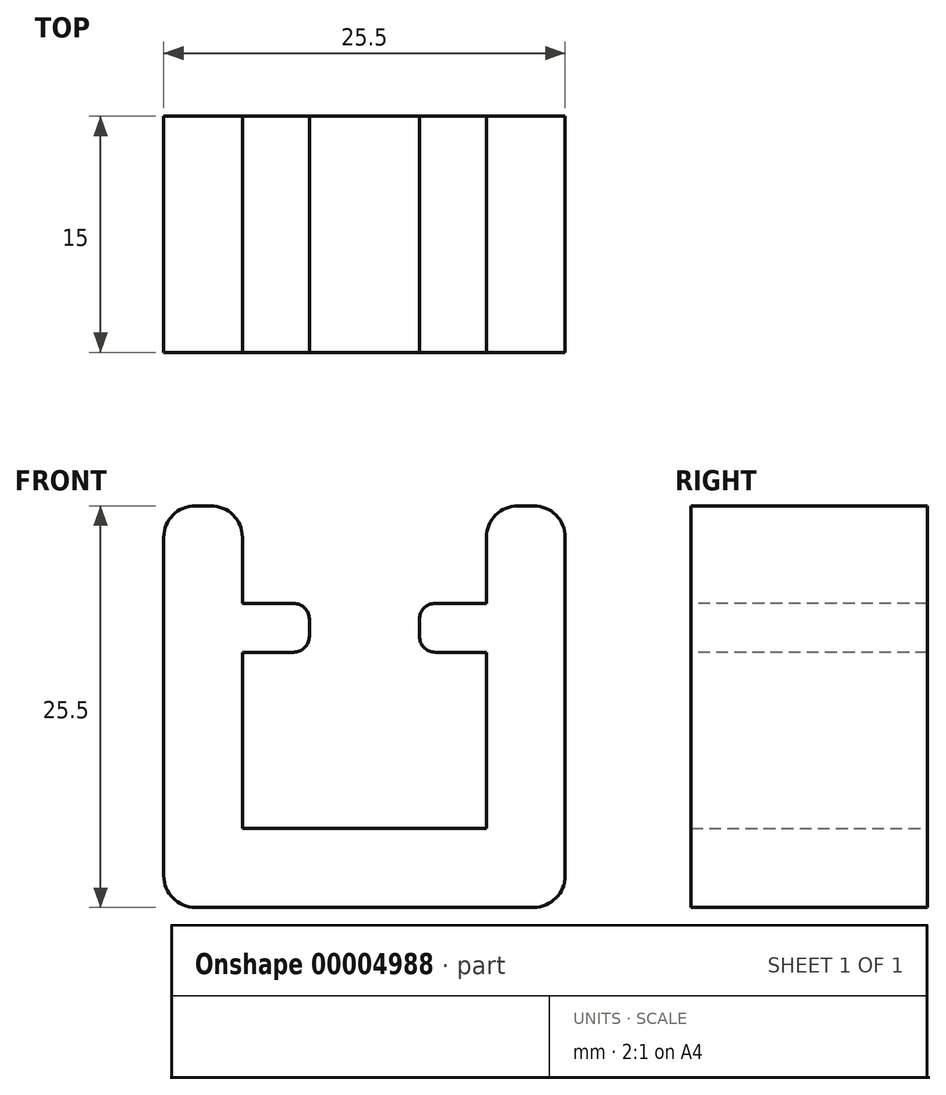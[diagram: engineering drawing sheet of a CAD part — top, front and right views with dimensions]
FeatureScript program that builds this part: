
annotation { "Feature Type Name" : "Feature", "Feature Type Description" : "" }
export const myFeature = defineFeature(function(context is Context, id is Id, definition is map)
    precondition{}
    {
        {
            var Q0;
            Q0=qCreatedBy(makeId("Front.planeOp"),FACE);
            var sketch = newSketch(context, id + "F0", { "sketchPlane" : qUnion([Q0])});
            skLineSegment(sketch, "E0", {"start": v(0, 0) * mm, "end": v(0, 15.32) * mm, "construction": true});
            skLineSegment(sketch, "E1.rect.bottom", {"start": v(7.75, 7.75) * mm, "end": v(-7.75, 7.75) * mm, "construction": true});
            skLineSegment(sketch, "E1.rect.top", {"start": v(7.75, -7.75) * mm, "end": v(-7.75, -7.75) * mm, "construction": true});
            skLineSegment(sketch, "E1.rect.left", {"start": v(7.75, 7.75) * mm, "end": v(7.75, -7.75) * mm});
            skLineSegment(sketch, "E1.rect.right", {"start": v(-7.75, 7.75) * mm, "end": v(-7.75, -7.75) * mm});
            skPoint(sketch, "E1.rect.middle", {"position": v(0, 0) * mm});
            skLineSegment(sketch, "E2", {"start": v(-7.75, 7.75) * mm, "end": v(-12.75, 7.75) * mm});
            skLineSegment(sketch, "E3", {"start": v(-12.75, 7.75) * mm, "end": v(-12.75, -17.75) * mm});
            skLineSegment(sketch, "E4", {"start": v(7.75, 7.75) * mm, "end": v(12.75, 7.75) * mm});
            skLineSegment(sketch, "E5", {"start": v(12.75, 7.75) * mm, "end": v(12.75, -17.75) * mm});
            skLineSegment(sketch, "E6", {"start": v(12.75, -17.75) * mm, "end": v(-12.75, -17.75) * mm});
            skLineSegment(sketch, "E7", {"start": v(-7.75, -7.75) * mm, "end": v(-7.75, -12.75) * mm});
            skLineSegment(sketch, "E8", {"start": v(-7.75, -12.75) * mm, "end": v(7.75, -12.75) * mm});
            skLineSegment(sketch, "E9", {"start": v(7.75, -12.75) * mm, "end": v(7.75, -7.75) * mm});
            skSolve(sketch);
        }
        {
            var Q0;
            Q0 = qSketchRegion(id + "F0", true);
            extrude(context, id + "F1", {"entities" : qUnion([Q0]), "depth" : 15 * mm});
        }
        {
            var Q0;
            Q0=makeQuery(id+"F1.opExtrude","CAP_FACE",FACE,{"disambiguationData":[OSD([sQuery(id+"F0.wireOp",EDGE,"E1.rect.left"),sQuery(id+"F0.wireOp",EDGE,"E1.rect.right"),sQuery(id+"F0.wireOp",EDGE,"E2"),sQuery(id+"F0.wireOp",EDGE,"E3"),sQuery(id+"F0.wireOp",EDGE,"E4"),sQuery(id+"F0.wireOp",EDGE,"E5"),sQuery(id+"F0.wireOp",EDGE,"E6"),sQuery(id+"F0.wireOp",EDGE,"E7"),sQuery(id+"F0.wireOp",EDGE,"E8"),sQuery(id+"F0.wireOp",EDGE,"E9")])],"isStart":false});
            var sketch = newSketch(context, id + "F2", { "sketchPlane" : qUnion([Q0])});
            skLineSegment(sketch, "E10", {"start": v(0, 0) * mm, "end": v(-7.75, 0) * mm, "construction": true});
            skLineSegment(sketch, "E11.bottom", {"start": v(-7.75, 1.55) * mm, "end": v(-3.5, 1.55) * mm});
            skLineSegment(sketch, "E11.top", {"start": v(-7.75, -1.55) * mm, "end": v(-3.5, -1.55) * mm});
            skLineSegment(sketch, "E11.left", {"start": v(-7.75, 1.55) * mm, "end": v(-7.75, -1.55) * mm});
            skLineSegment(sketch, "E11.right", {"start": v(-3.5, 1.55) * mm, "end": v(-3.5, -1.55) * mm});
            skPoint(sketch, "E12", {"position": v(-3.5, 0) * mm});
            skLineSegment(sketch, "E13", {"start": v(0, 0) * mm, "end": v(0, 15.8) * mm, "construction": true});
            skLineSegment(sketch, "E14.0.MirrorCS", {"start": v(7.75, -1.55) * mm, "end": v(3.5, -1.55) * mm});
            skLineSegment(sketch, "E14.1.MirrorCS", {"start": v(3.5, 1.55) * mm, "end": v(3.5, -1.55) * mm});
            skLineSegment(sketch, "E14.2.MirrorCS", {"start": v(7.75, 1.55) * mm, "end": v(7.75, -1.55) * mm});
            skLineSegment(sketch, "E14.3.MirrorCS", {"start": v(7.75, 1.55) * mm, "end": v(3.5, 1.55) * mm});
            skSolve(sketch);
        }
        {
            var Q0;
            Q0 = qSketchRegion(id + "F2", true);
            var Q1;
            Q1=makeQuery(id+"F1.opExtrude","CAP_FACE",FACE,{"disambiguationData":[OSD([sQuery(id+"F0.wireOp",EDGE,"E1.rect.left"),sQuery(id+"F0.wireOp",EDGE,"E1.rect.right"),sQuery(id+"F0.wireOp",EDGE,"E2"),sQuery(id+"F0.wireOp",EDGE,"E3"),sQuery(id+"F0.wireOp",EDGE,"E4"),sQuery(id+"F0.wireOp",EDGE,"E5"),sQuery(id+"F0.wireOp",EDGE,"E6"),sQuery(id+"F0.wireOp",EDGE,"E7"),sQuery(id+"F0.wireOp",EDGE,"E8"),sQuery(id+"F0.wireOp",EDGE,"E9")])],"isStart":true});
            extrude(context, id + "F3", {"entities" : qUnion([Q0]), "operationType" : NewBodyOperationType.ADD, "endBound" : BoundingType.UP_TO_SURFACE, "oppositeDirection" : true, "endBoundEntityFace" : qUnion([Q1]), "depth" : 25 * mm});
        }
        {
            var Q0;
            Q0=makeQuery(id+"F1.opExtrude","SWEPT_EDGE",EDGE,{"disambiguationData":[OSD([sQuery(id+"F0.wireOp",EDGE,"E3"),sQuery(id+"F0.wireOp",EDGE,"E6")])]});
            var Q1;
            Q1=makeQuery(id+"F1.opExtrude","SWEPT_EDGE",EDGE,{"disambiguationData":[OSD([sQuery(id+"F0.wireOp",EDGE,"E5"),sQuery(id+"F0.wireOp",EDGE,"E6")])]});
            var Q2;
            Q2=makeQuery(id+"F1.opExtrude","SWEPT_EDGE",EDGE,{"disambiguationData":[OSD([sQuery(id+"F0.wireOp",EDGE,"E4"),sQuery(id+"F0.wireOp",EDGE,"E5")])]});
            var Q3;
            Q3=makeQuery(id+"F1.opExtrude","SWEPT_EDGE",EDGE,{"disambiguationData":[OSD([sQuery(id+"F0.wireOp",EDGE,"E2"),sQuery(id+"F0.wireOp",EDGE,"E3")])]});
            var Q4;
            Q4=makeQuery(id+"F1.opExtrude","SWEPT_EDGE",EDGE,{"disambiguationData":[OSD([sQuery(id+"F0.wireOp",EDGE,"E1.rect.left"),sQuery(id+"F0.wireOp",EDGE,"E4")])]});
            var Q5;
            Q5=makeQuery(id+"F1.opExtrude","SWEPT_EDGE",EDGE,{"disambiguationData":[OSD([sQuery(id+"F0.wireOp",EDGE,"E1.rect.right"),sQuery(id+"F0.wireOp",EDGE,"E2")])]});
            fillet(context, id + "F4", {"entities" : qUnion([Q0, Q1, Q2, Q3, Q4, Q5]), "radius" : 2 * mm, "tangentPropagation" : true, "allowEdgeOverflow" : false});
        }
        {
            var Q0;
            Q0=makeQuery(id+"F3.opExtrude","SWEPT_EDGE",EDGE,{"disambiguationData":[OSD([sQuery(id+"F2.wireOp",EDGE,"E11.bottom"),sQuery(id+"F2.wireOp",EDGE,"E11.right")])]});
            var Q1;
            Q1=makeQuery(id+"F3.opExtrude","SWEPT_EDGE",EDGE,{"disambiguationData":[OSD([sQuery(id+"F2.wireOp",EDGE,"E11.top"),sQuery(id+"F2.wireOp",EDGE,"E11.right")])]});
            var Q2;
            Q2=makeQuery(id+"F3.opExtrude","SWEPT_EDGE",EDGE,{"disambiguationData":[OSD([sQuery(id+"F2.wireOp",EDGE,"E14.1.MirrorCS"),sQuery(id+"F2.wireOp",EDGE,"E14.3.MirrorCS")])]});
            var Q3;
            Q3=makeQuery(id+"F3.opExtrude","SWEPT_EDGE",EDGE,{"disambiguationData":[OSD([sQuery(id+"F2.wireOp",EDGE,"E14.0.MirrorCS"),sQuery(id+"F2.wireOp",EDGE,"E14.1.MirrorCS")])]});
            fillet(context, id + "F5", {"entities" : qUnion([Q0, Q1, Q2, Q3]), "radius" : 1 * mm, "tangentPropagation" : true, "allowEdgeOverflow" : false});
        }
    });
